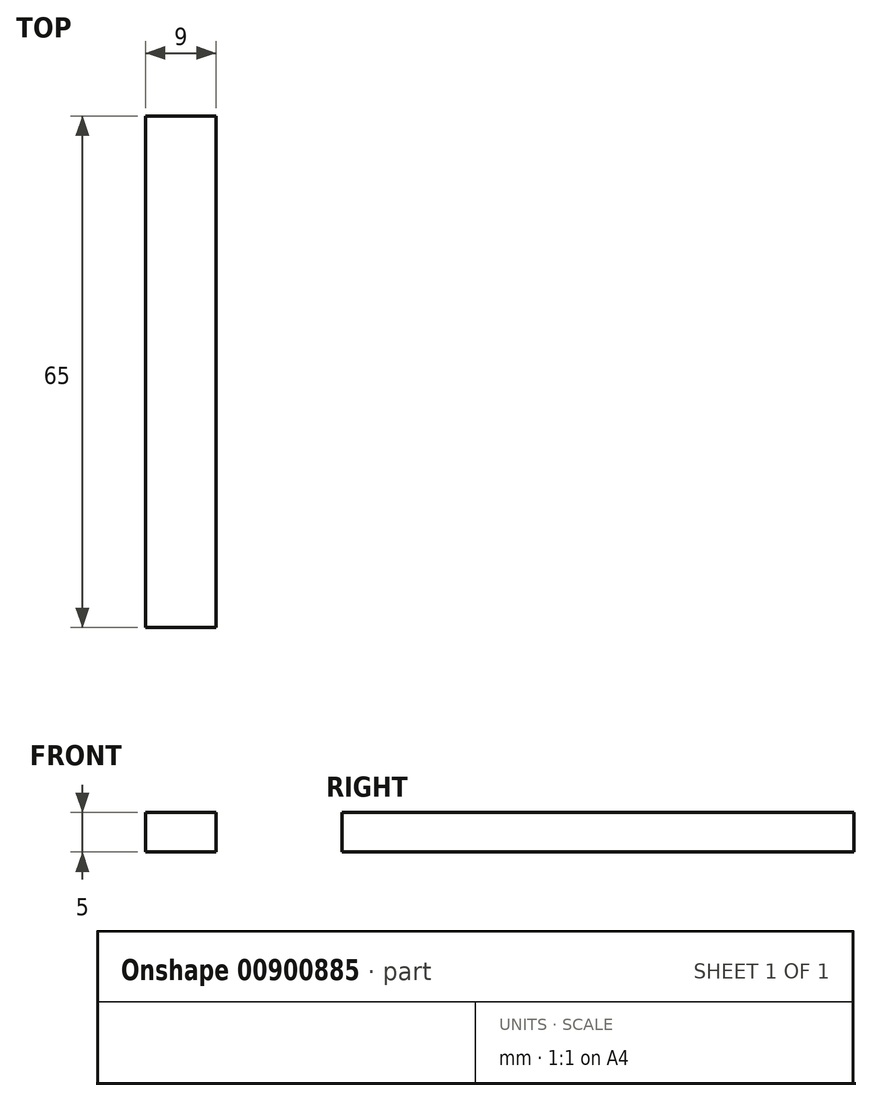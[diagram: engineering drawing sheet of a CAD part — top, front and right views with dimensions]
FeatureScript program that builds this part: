
annotation { "Feature Type Name" : "Feature", "Feature Type Description" : "" }
export const myFeature = defineFeature(function(context is Context, id is Id, definition is map)
    precondition{}
    {
        {
            var Q0;
            Q0=qCreatedBy(makeId("Top.planeOp"),FACE);
            var sketch = newSketch(context, id + "F0", { "sketchPlane" : qUnion([Q0])});
            skLineSegment(sketch, "E0.bottom", {"start": v(0, 0) * mm, "end": v(-9, 0) * mm});
            skLineSegment(sketch, "E0.top", {"start": v(0, 65) * mm, "end": v(-9, 65) * mm});
            skLineSegment(sketch, "E0.left", {"start": v(0, 0) * mm, "end": v(0, 65) * mm});
            skLineSegment(sketch, "E0.right", {"start": v(-9, 0) * mm, "end": v(-9, 65) * mm});
            skSolve(sketch);
        }
        {
            var Q0;
            Q0=qSketchRegion(id+"F0",true);
            extrude(context, id + "F1", {"entities" : qUnion([Q0]), "depth" : 5 * mm, "offsetDistance" : 25 * mm});
        }
    });
